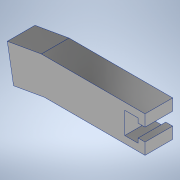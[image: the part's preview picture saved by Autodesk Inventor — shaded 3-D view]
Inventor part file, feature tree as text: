
AUTODESK INVENTOR PART (.ipt)
format: ipt  version: 2022 (Build 260153000, 153)  size: 149,504 bytes
history: native  units: mm
features: extrude x3, sketch x3
ambient origin geometry x8: Origin, YZ Plane, XZ Plane, XY Plane, X Axis, Y Axis, Z Axis, Center Point
bodies: Body1 (feature_tree)
feature tree (6):
  extrude  "Extrusion2"  Depth=5.8mm
  extrude  "Extrusion4"  Depth=12.0mm TaperAngle=0.0deg
  extrude  "Extrusion5"  Depth=15.6mm
  sketch  "Sketch5"  dims[d41=5.8mm d48=44.0mm]
  sketch  "Sketch7"  dims[d50=3.0mm d56=12.0mm d57=0.0mm]
  sketch  "Sketch9"  dims[d63=45.0mm d67=15.6mm d71=0.0mm d72=36.2mm d78=0.0mm d79=0.0mm d80=5.6mm d81=9.5mm d83=15.6mm d84=1.745329mm d85=90.0deg d86=1.745329mm d87=15.0mm d88=0.0mm d89=0.0mm]
